# Revit family: SDD75X133
name_source: partatom
category: Structural Connections
revit_build: Autodesk Revit 2015 (Build: 20140606_1530(x64)
units: mm (PartAtom-declared; Revit-internal decimal feet)

## types (1)
- SDD75X133
    Default Elevation = 0 mm  [stored 0 ft]
    Density = 0.05 kg
    Description = Self-Drilling Dowel
    EPD = https://www.strongtie.eu
    ETA / DoP = https://www.strongtie.eu
    Manufacturer = Simpson Strong-Tie
    Model = SDD7.5X133
    Model Disclaimer = Contact Simpson Strong-Tie Company  for more information
    Model ID = 0119470708918108315928591517815896633941
    Name = SDD7.5X133
    ObjectType = SDD7.5X133
    Product Material = ElectroGalvanised
    Product Type = Self-Drilling Dowel
    Reference = 78121
    Technical datasheet = https://www.strongtie.eu
    URL = www.strongtie.eu
    UniClass Number = Pr_20_29_76_76
    UniClass Title = Self-drilling screws

note: [stored X ft] marks values corroborated as IEEE doubles in the binary element streams (Revit-internal decimal feet)

## geometry (parser evidence)
native form markers: Blend x24, Sweep x3
no freeform markers — native parametric forms only
